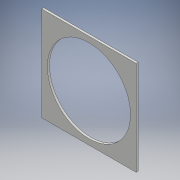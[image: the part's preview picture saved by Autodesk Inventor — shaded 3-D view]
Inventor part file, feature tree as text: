
AUTODESK INVENTOR PART (.ipt)
format: ipt  version: 2018 (Build 220112000, 112)  size: 103,936 bytes
history: native  units: mm
features: extrude x2, sketch x2
ambient origin geometry x8: Origin, YZ Plane, XZ Plane, XY Plane, X Axis, Y Axis, Z Axis, Center Point
bodies: Solid1 (feature_tree)
feature tree (4):
  extrude  "Extrusion1"  Depth=110.0mm
  extrude  "Extrusion2"  Depth=2.5mm TaperAngle=0.0deg
  sketch  "Sketch1"  dims[d0=110.0mm d1=110.0mm]
  sketch  "Sketch2"  dims[d2=2.5mm d3=0.0mm d5=2.5mm d6=0.0mm]
